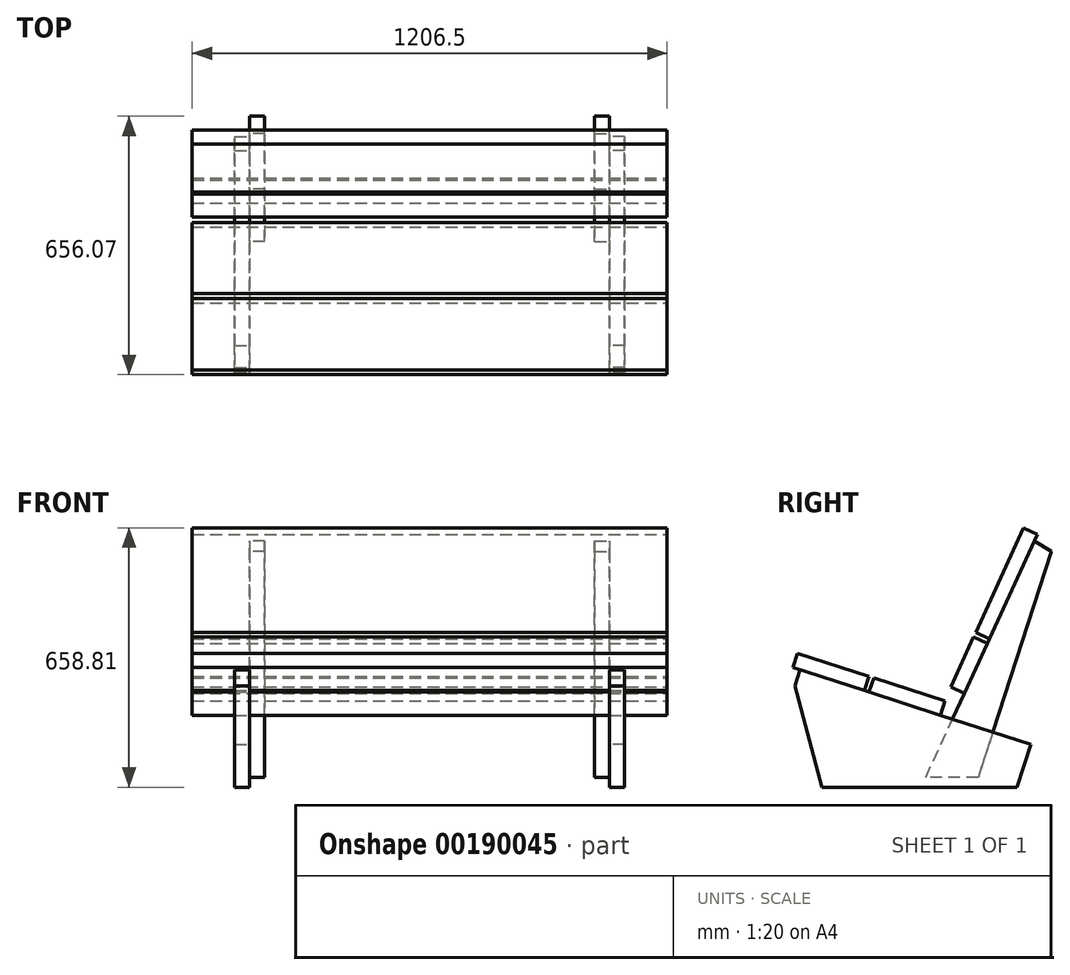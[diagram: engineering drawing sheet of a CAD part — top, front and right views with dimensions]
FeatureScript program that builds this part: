
annotation { "Feature Type Name" : "Feature", "Feature Type Description" : "" }
export const myFeature = defineFeature(function(context is Context, id is Id, definition is map)
    precondition{}
    {
        {
            var Q0;
            Q0=qCreatedBy(makeId("Right.planeOp"),FACE);
            var sketch = newSketch(context, id + "F0", { "sketchPlane" : qUnion([Q0])});
            skLineSegment(sketch, "E0", {"start": v(0, 0) * mm, "end": v(495.3, 0) * mm});
            skLineSegment(sketch, "E1", {"start": v(495.3, 0) * mm, "end": v(530.47, 108.75) * mm});
            skLineSegment(sketch, "E2", {"start": v(530.47, 108.75) * mm, "end": v(-55.6, 298.28) * mm});
            skLineSegment(sketch, "E3", {"start": v(-55.6, 298.28) * mm, "end": v(-68.72, 257.7) * mm});
            skLineSegment(sketch, "E4", {"start": v(-68.72, 257.7) * mm, "end": v(0, 0) * mm});
            skSolve(sketch);
        }
        {
            var Q0;
            Q0 = qSketchRegion(id + "F0", true);
            extrude(context, id + "F1", {"entities" : qUnion([Q0]), "depth" : 38.1 * mm});
        }
        {
            var Q0;
            Q0=makeQuery(id+"F1.opExtrude","CAP_FACE",FACE,{"disambiguationData":[OSD([sQuery(id+"F0.wireOp",EDGE,"E0"),sQuery(id+"F0.wireOp",EDGE,"E1"),sQuery(id+"F0.wireOp",EDGE,"E2"),sQuery(id+"F0.wireOp",EDGE,"E3"),sQuery(id+"F0.wireOp",EDGE,"E4")])],"isStart":true});
            var sketch = newSketch(context, id + "F2", { "sketchPlane" : qUnion([Q0])});
            skLineSegment(sketch, "E5", {"start": v(-263.38, 25.4) * mm, "end": v(-538.84, 625.6) * mm});
            skLineSegment(sketch, "E6", {"start": v(-538.84, 625.6) * mm, "end": v(-582.35, 599.38) * mm});
            skLineSegment(sketch, "E7", {"start": v(-582.35, 599.38) * mm, "end": v(-396.73, 25.4) * mm});
            skLineSegment(sketch, "E8", {"start": v(-396.73, 25.4) * mm, "end": v(-263.38, 25.4) * mm});
            skSolve(sketch);
        }
        {
            var Q0;
            {var subQ0=sQuery(id+"F2.wireOp",EDGE,"E6");Q0=makeQuery(id+"F2.imprint","IMPRINT",FACE,{"disambiguationData":[TD([[makeQuery(id+"F2.imprint","IMPRINT",EDGE,{"derivedFrom":subQ0}),1.0]])]});}
            var Q1;
            {var subQ0=sQuery(id+"F2.wireOp",EDGE,"E8");Q1=makeQuery(id+"F2.imprint","IMPRINT",FACE,{"disambiguationData":[TD([[makeQuery(id+"F2.imprint","IMPRINT",EDGE,{"derivedFrom":subQ0}),1.0]])]});}
            extrude(context, id + "F3", {"entities" : qUnion([Q0, Q1]), "depth" : 38.1 * mm});
        }
        {
            var Q0;
            Q0=qCreatedBy(makeId("Right.planeOp"),FACE);
            cPlane(context, id + "F4", {"entities" : qUnion([Q0]), "cplaneType" : CPlaneType.OFFSET, "offset" : 457.2 * mm, "oppositeDirection" : true, "width" : 152.4 * mm, "height" : 152.4 * mm});
        }
        {
            var Q0;
            Q0=makeQuery(id+"F1.opExtrude","SWEPT_BODY",BODY,{"disambiguationData":[OSD([sQuery(id+"F0.wireOp",EDGE,"E0"),sQuery(id+"F0.wireOp",EDGE,"E1"),sQuery(id+"F0.wireOp",EDGE,"E2"),sQuery(id+"F0.wireOp",EDGE,"E3"),sQuery(id+"F0.wireOp",EDGE,"E4")])]});
            var Q1;
            Q1=makeQuery(id+"F3.opExtrude","SWEPT_BODY",BODY,{"disambiguationData":[OSD([sQuery(id+"F2.wireOp",EDGE,"E5"),sQuery(id+"F2.wireOp",EDGE,"E6"),sQuery(id+"F2.wireOp",EDGE,"E7"),sQuery(id+"F2.wireOp",EDGE,"E8")])]});
            var Q2;
            Q2=qCreatedBy(id+"F4.planeOp",FACE);
            mirror(context, id + "F5", {"entities" : qUnion([Q0, Q1]), "mirrorPlane" : qUnion([Q2])});
        }
        {
            var Q0;
            Q0=makeQuery(id+"F3.opExtrude","SWEPT_FACE",FACE,{"disambiguationData":[OSD([sQuery(id+"F2.wireOp",EDGE,"E5")])]});
            var sketch = newSketch(context, id + "F6", { "sketchPlane" : qUnion([Q0])});
            skLineSegment(sketch, "E9.bottom", {"start": v(-1060.45, 812.4) * mm, "end": v(146.05, 812.4) * mm});
            skLineSegment(sketch, "E9.top", {"start": v(-1060.45, 520.3) * mm, "end": v(146.05, 520.3) * mm});
            skLineSegment(sketch, "E9.left", {"start": v(-1060.45, 812.4) * mm, "end": v(-1060.45, 520.3) * mm});
            skLineSegment(sketch, "E9.right", {"start": v(146.05, 812.4) * mm, "end": v(146.05, 520.3) * mm});
            skLineSegment(sketch, "E10.bottom", {"start": v(-1060.45, 507.6) * mm, "end": v(146.05, 507.6) * mm});
            skLineSegment(sketch, "E10.top", {"start": v(-1060.45, 367.9) * mm, "end": v(146.05, 367.9) * mm});
            skLineSegment(sketch, "E10.left", {"start": v(-1060.45, 507.6) * mm, "end": v(-1060.45, 367.9) * mm});
            skLineSegment(sketch, "E11", {"start": v(146.05, 507.6) * mm, "end": v(146.05, 367.9) * mm});
            skSolve(sketch);
        }
        {
            var Q0;
            Q0=makeQuery(id+"F6.imprint","IMPRINT",FACE,{"disambiguationData":[TD([[makeQuery(id+"F6.imprint","IMPRINT",EDGE,{"derivedFrom":sQuery(id+"F6.wireOp",EDGE,"E9.bottom")}),-1.0]])]});
            var Q1;
            {var subQ0=sQuery(id+"F6.wireOp",EDGE,"E10.left");Q1=makeQuery(id+"F6.imprint","IMPRINT",FACE,{"disambiguationData":[TD([[makeQuery(id+"F6.imprint","IMPRINT",EDGE,{"derivedFrom":subQ0}),1.0]])]});}
            var Q2;
            {var subQ0=sQuery(id+"F6.wireOp",EDGE,"E11");Q2=makeQuery(id+"F6.imprint","IMPRINT",FACE,{"disambiguationData":[TD([[makeQuery(id+"F6.imprint","IMPRINT",EDGE,{"derivedFrom":subQ0}),-1.0]])]});}
            var Q3;
            {var subQ0=sQuery(id+"F6.wireOp",EDGE,"E10.bottom");var subQ1=sQuery(id+"F2.wireOp",EDGE,"E5");var subQ2=makeQuery(id+"F3.opExtrude","CAP_EDGE",EDGE,{"disambiguationData":[OSD([subQ1])],"isStart":false});var subQ3=makeQuery(id+"F6.imprint","INTERSECT",VERTEX,{"derivedFrom":[subQ2,subQ0]});Q3=makeQuery(id+"F6.imprint","IMPRINT",FACE,{"disambiguationData":[TD([[makeQuery(id+"F6.imprint","IMPRINT",EDGE,{"disambiguationData":[TD([[subQ3,-1.0]])],"derivedFrom":subQ0}),-1.0]])]});}
            var Q4;
            {var subQ1=sQuery(id+"F2.wireOp",EDGE,"E5");var subQ6=makeQuery(id+"F3.opExtrude","SWEPT_EDGE",EDGE,{"disambiguationData":[OSD([subQ1,sQuery(id+"F2.wireOp",EDGE,"E6")])]});Q4=makeQuery(id+"F6.imprint","IMPRINT",FACE,{"disambiguationData":[TD([[makeQuery(id+"F6.imprint","IMPRINT",EDGE,{"derivedFrom":subQ6}),-1.0]])]});}
            extrude(context, id + "F7", {"entities" : qUnion([Q0, Q1, Q2, Q3, Q4]), "depth" : 38.1 * mm});
        }
        {
            var Q0;
            Q0=makeQuery(id+"F1.opExtrude","SWEPT_FACE",FACE,{"disambiguationData":[OSD([sQuery(id+"F0.wireOp",EDGE,"E2")])]});
            var sketch = newSketch(context, id + "F8", { "sketchPlane" : qUnion([Q0])});
            skLineSegment(sketch, "E12.bottom", {"start": v(-1060.45, -163.73) * mm, "end": v(146.05, -163.73) * mm});
            skLineSegment(sketch, "E12.top", {"start": v(-1060.45, 26.77) * mm, "end": v(146.05, 26.77) * mm});
            skLineSegment(sketch, "E12.left", {"start": v(-1060.45, -163.73) * mm, "end": v(-1060.45, 26.77) * mm});
            skLineSegment(sketch, "E12.right", {"start": v(146.05, -163.73) * mm, "end": v(146.05, 26.77) * mm});
            skLineSegment(sketch, "E13.bottom", {"start": v(-1060.45, 39.47) * mm, "end": v(146.05, 39.47) * mm});
            skLineSegment(sketch, "E13.top", {"start": v(-1060.45, 229.97) * mm, "end": v(146.05, 229.97) * mm});
            skLineSegment(sketch, "E13.left", {"start": v(-1060.45, 39.47) * mm, "end": v(-1060.45, 229.97) * mm});
            skLineSegment(sketch, "E13.right", {"start": v(146.05, 39.47) * mm, "end": v(146.05, 229.97) * mm});
            skSolve(sketch);
        }
        {
            var Q0;
            Q0=makeQuery(id+"F8.imprint","IMPRINT",FACE,{"disambiguationData":[TD([[makeQuery(id+"F8.imprint","IMPRINT",EDGE,{"derivedFrom":sQuery(id+"F8.wireOp",EDGE,"E12.bottom")}),1.0]])]});
            var Q1;
            {var subQ0=sQuery(id+"F8.wireOp",EDGE,"E13.left");Q1=makeQuery(id+"F8.imprint","IMPRINT",FACE,{"disambiguationData":[TD([[makeQuery(id+"F8.imprint","IMPRINT",EDGE,{"derivedFrom":subQ0}),-1.0]])]});}
            var Q2;
            {var subQ0=sQuery(id+"F8.wireOp",EDGE,"E13.right");Q2=makeQuery(id+"F8.imprint","IMPRINT",FACE,{"disambiguationData":[TD([[makeQuery(id+"F8.imprint","IMPRINT",EDGE,{"derivedFrom":subQ0}),1.0]])]});}
            var Q3;
            {var subQ0=sQuery(id+"F8.wireOp",EDGE,"E13.bottom");var subQ1=sQuery(id+"F0.wireOp",EDGE,"E2");var subQ2=makeQuery(id+"F1.opExtrude","CAP_EDGE",EDGE,{"disambiguationData":[OSD([subQ1])],"isStart":true});var subQ3=makeQuery(id+"F8.imprint","INTERSECT",VERTEX,{"derivedFrom":[subQ2,subQ0]});Q3=makeQuery(id+"F8.imprint","IMPRINT",FACE,{"disambiguationData":[TD([[makeQuery(id+"F8.imprint","IMPRINT",EDGE,{"disambiguationData":[TD([[subQ3,-1.0]])],"derivedFrom":subQ0}),1.0]])]});}
            var Q4;
            {var subQ1=sQuery(id+"F0.wireOp",EDGE,"E2");var subQ6=makeQuery(id+"F1.opExtrude","SWEPT_EDGE",EDGE,{"disambiguationData":[OSD([subQ1,sQuery(id+"F0.wireOp",EDGE,"E3")])]});Q4=makeQuery(id+"F8.imprint","IMPRINT",FACE,{"disambiguationData":[TD([[makeQuery(id+"F8.imprint","IMPRINT",EDGE,{"derivedFrom":subQ6}),-1.0]])]});}
            extrude(context, id + "F9", {"entities" : qUnion([Q0, Q1, Q2, Q3, Q4]), "depth" : 38.1 * mm});
        }
    });
